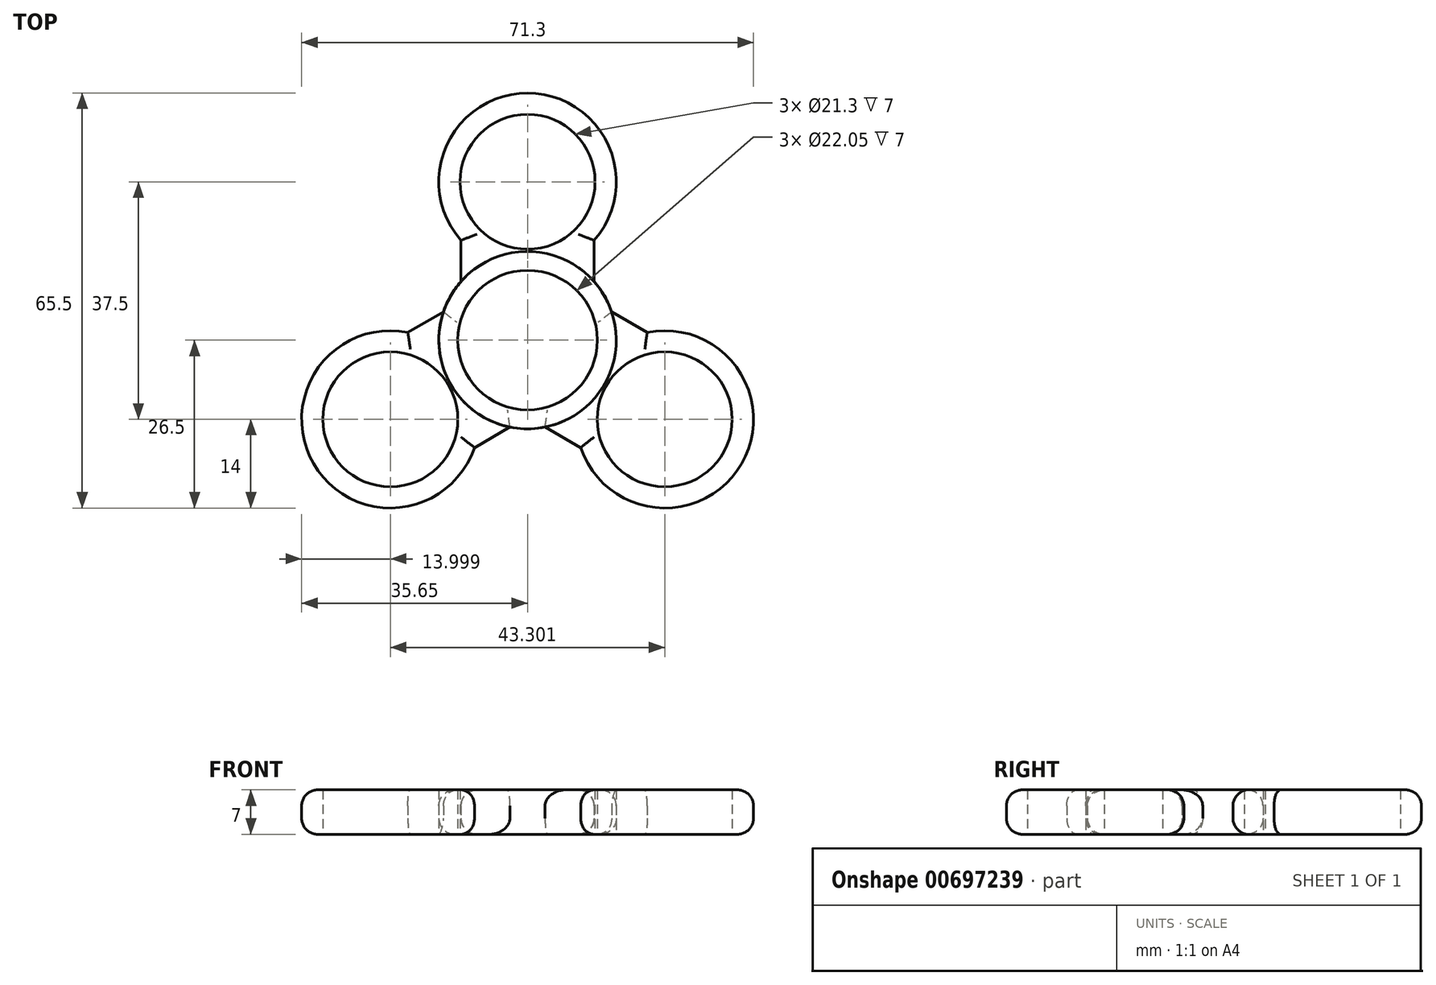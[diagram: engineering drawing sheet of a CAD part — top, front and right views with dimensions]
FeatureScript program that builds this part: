
annotation { "Feature Type Name" : "Feature", "Feature Type Description" : "" }
export const myFeature = defineFeature(function(context is Context, id is Id, definition is map)
    precondition{}
    {
        {
            var Q0;
            Q0=qCreatedBy(makeId("Top.planeOp"),FACE);
            var sketch = newSketch(context, id + "F0", { "sketchPlane" : qUnion([Q0])});
            skCircle(sketch, "E0", {"center": v(0, 0) * mm, "radius": 10.65 * mm});
            skCircle(sketch, "E1", {"center": v(0, -25) * mm, "radius": 11.03 * mm});
            skCircle(sketch, "E2", {"center": v(0, 0) * mm, "radius": 14 * mm});
            skCircle(sketch, "E3", {"center": v(0, -25) * mm, "radius": 14 * mm});
            skLineSegment(sketch, "E4", {"start": v(-10.5, -9.25) * mm, "end": v(-10.5, -15.75) * mm});
            skLineSegment(sketch, "E5", {"start": v(10.5, -9.25) * mm, "end": v(10.5, -15.75) * mm});
            skSolve(sketch);
        }
        {
            var Q0;
            Q0=qSketchRegion(id+"F0",true);
            var Q1;
            {var subQ3=sQuery(id+"F0.wireOp",EDGE,"E3");var subQ6=sQuery(id+"F0.wireOp",EDGE,"E0");var subQ9=makeQuery(id+"F0.imprint","INTERSECT",VERTEX,{"disambiguationData":[OD(0.0)],"derivedFrom":[subQ6,subQ3]});Q1=makeQuery(id+"F0.imprint","IMPRINT",FACE,{"disambiguationData":[TD([[makeQuery(id+"F0.imprint","IMPRINT",EDGE,{"disambiguationData":[TD([[subQ9,1.0]])],"derivedFrom":subQ6}),-1.0]])]});}
            var Q2;
            {var subQ0=sQuery(id+"F0.wireOp",EDGE,"E3");var subQ1=sQuery(id+"F0.wireOp",EDGE,"E2");var subQ2=makeQuery(id+"F0.imprint","INTERSECT",VERTEX,{"disambiguationData":[OD(0.0)],"derivedFrom":[subQ1,subQ0]});Q2=makeQuery(id+"F0.imprint","IMPRINT",FACE,{"disambiguationData":[TD([[makeQuery(id+"F0.imprint","IMPRINT",EDGE,{"disambiguationData":[TD([[subQ2,-1.0]])],"derivedFrom":subQ1}),1.0]])]});}
            extrude(context, id + "F1", {"entities" : qUnion([Q0, Q1, Q2]), "depth" : 7 * mm, "offsetDistance" : 25 * mm});
        }
        {
            var Q0;
            Q0=makeQuery(id+"F1.opExtrude","SWEPT_BODY",BODY,{"disambiguationData":[OSD([sQuery(id+"F0.wireOp",EDGE,"E0"),sQuery(id+"F0.wireOp",EDGE,"E1"),sQuery(id+"F0.wireOp",EDGE,"E2"),sQuery(id+"F0.wireOp",EDGE,"E3"),sQuery(id+"F0.wireOp",EDGE,"E4"),sQuery(id+"F0.wireOp",EDGE,"E5")])]});
            var Q1;
            Q1=makeQuery(id+"F1.opExtrude","SWEPT_FACE",FACE,{"disambiguationData":[OSD([sQuery(id+"F0.wireOp",EDGE,"E3")])]});
            circularPattern(context, id + "F2", {"entities" : qUnion([Q0]), "axis" : qUnion([Q1]), "angle" : 360 * degree, "instanceCount" : 3, "equalSpace" : true});
        }
        {
            var Q0;
            Q0=makeQuery(id+"F2.opPattern","COPY",EDGE,{"derivedFrom":makeQuery(id+"F1.opExtrude","CAP_EDGE",EDGE,{"disambiguationData":[OSD([sQuery(id+"F0.wireOp",EDGE,"E2")])],"isStart":false}),"instanceName":"2"});
            var Q1;
            Q1=makeQuery(id+"F2.opPattern","COPY",EDGE,{"derivedFrom":makeQuery(id+"F1.opExtrude","CAP_EDGE",EDGE,{"disambiguationData":[OSD([sQuery(id+"F0.wireOp",EDGE,"E2")])],"isStart":false}),"instanceName":"1"});
            var Q2;
            Q2=makeQuery(id+"F2.opPattern","COPY",EDGE,{"derivedFrom":makeQuery(id+"F1.opExtrude","CAP_EDGE",EDGE,{"disambiguationData":[OSD([sQuery(id+"F0.wireOp",EDGE,"E4")])],"isStart":false}),"instanceName":"2"});
            var Q3;
            Q3=makeQuery(id+"F2.opPattern","COPY",EDGE,{"derivedFrom":makeQuery(id+"F1.opExtrude","CAP_EDGE",EDGE,{"disambiguationData":[OSD([sQuery(id+"F0.wireOp",EDGE,"E5")])],"isStart":false}),"instanceName":"1"});
            var Q4;
            Q4=makeQuery(id+"F2.opPattern","COPY",EDGE,{"derivedFrom":makeQuery(id+"F1.opExtrude","CAP_EDGE",EDGE,{"disambiguationData":[OSD([sQuery(id+"F0.wireOp",EDGE,"E4")])],"isStart":false}),"instanceName":"1"});
            var Q5;
            Q5=makeQuery(id+"F1.opExtrude","CAP_EDGE",EDGE,{"disambiguationData":[OSD([sQuery(id+"F0.wireOp",EDGE,"E5")])],"isStart":false});
            var Q6;
            Q6=makeQuery(id+"F1.opExtrude","CAP_EDGE",EDGE,{"disambiguationData":[OSD([sQuery(id+"F0.wireOp",EDGE,"E2")])],"isStart":true});
            var Q7;
            Q7=makeQuery(id+"F1.opExtrude","CAP_EDGE",EDGE,{"disambiguationData":[OSD([sQuery(id+"F0.wireOp",EDGE,"E2")])],"isStart":false});
            var Q8;
            Q8=makeQuery(id+"F1.opExtrude","CAP_EDGE",EDGE,{"disambiguationData":[OSD([sQuery(id+"F0.wireOp",EDGE,"E4")])],"isStart":false});
            var Q9;
            Q9=makeQuery(id+"F2.opPattern","COPY",EDGE,{"derivedFrom":makeQuery(id+"F1.opExtrude","CAP_EDGE",EDGE,{"disambiguationData":[OSD([sQuery(id+"F0.wireOp",EDGE,"E5")])],"isStart":false}),"instanceName":"2"});
            var Q10;
            Q10=makeQuery(id+"F2.opPattern","COPY",EDGE,{"derivedFrom":makeQuery(id+"F1.opExtrude","CAP_EDGE",EDGE,{"disambiguationData":[OSD([sQuery(id+"F0.wireOp",EDGE,"E4")])],"isStart":true}),"instanceName":"2"});
            var Q11;
            Q11=makeQuery(id+"F2.opPattern","COPY",EDGE,{"derivedFrom":makeQuery(id+"F1.opExtrude","CAP_EDGE",EDGE,{"disambiguationData":[OSD([sQuery(id+"F0.wireOp",EDGE,"E5")])],"isStart":true}),"instanceName":"1"});
            var Q12;
            Q12=makeQuery(id+"F2.opPattern","COPY",EDGE,{"derivedFrom":makeQuery(id+"F1.opExtrude","CAP_EDGE",EDGE,{"disambiguationData":[OSD([sQuery(id+"F0.wireOp",EDGE,"E2")])],"isStart":true}),"instanceName":"1"});
            var Q13;
            Q13=makeQuery(id+"F2.opPattern","COPY",EDGE,{"derivedFrom":makeQuery(id+"F1.opExtrude","CAP_EDGE",EDGE,{"disambiguationData":[OSD([sQuery(id+"F0.wireOp",EDGE,"E4")])],"isStart":true}),"instanceName":"1"});
            var Q14;
            Q14=makeQuery(id+"F2.opPattern","COPY",EDGE,{"derivedFrom":makeQuery(id+"F1.opExtrude","CAP_EDGE",EDGE,{"disambiguationData":[OSD([sQuery(id+"F0.wireOp",EDGE,"E2")])],"isStart":true}),"instanceName":"2"});
            var Q15;
            Q15=makeQuery(id+"F2.opPattern","COPY",EDGE,{"derivedFrom":makeQuery(id+"F1.opExtrude","CAP_EDGE",EDGE,{"disambiguationData":[OSD([sQuery(id+"F0.wireOp",EDGE,"E5")])],"isStart":true}),"instanceName":"2"});
            var Q16;
            Q16=makeQuery(id+"F1.opExtrude","CAP_EDGE",EDGE,{"disambiguationData":[OSD([sQuery(id+"F0.wireOp",EDGE,"E4")])],"isStart":true});
            var Q17;
            Q17=makeQuery(id+"F1.opExtrude","CAP_EDGE",EDGE,{"disambiguationData":[OSD([sQuery(id+"F0.wireOp",EDGE,"E5")])],"isStart":true});
            var Q18;
            Q18=makeQuery(id+"F2.opPattern","COPY",EDGE,{"derivedFrom":makeQuery(id+"F1.opExtrude","CAP_EDGE",EDGE,{"disambiguationData":[OSD([sQuery(id+"F0.wireOp",EDGE,"E3")])],"isStart":false}),"instanceName":"2"});
            var Q19;
            Q19=makeQuery(id+"F2.opPattern","COPY",EDGE,{"derivedFrom":makeQuery(id+"F1.opExtrude","CAP_EDGE",EDGE,{"disambiguationData":[OSD([sQuery(id+"F0.wireOp",EDGE,"E3")])],"isStart":true}),"instanceName":"1"});
            fillet(context, id + "F3", {"entities" : qUnion([Q0, Q1, Q2, Q3, Q4, Q5, Q6, Q7, Q8, Q9, Q10, Q11, Q12, Q13, Q14, Q15, Q16, Q17, Q18, Q19]), "radius" : 2.5 * mm, "tangentPropagation" : true, "allowEdgeOverflow" : false});
        }
    });
